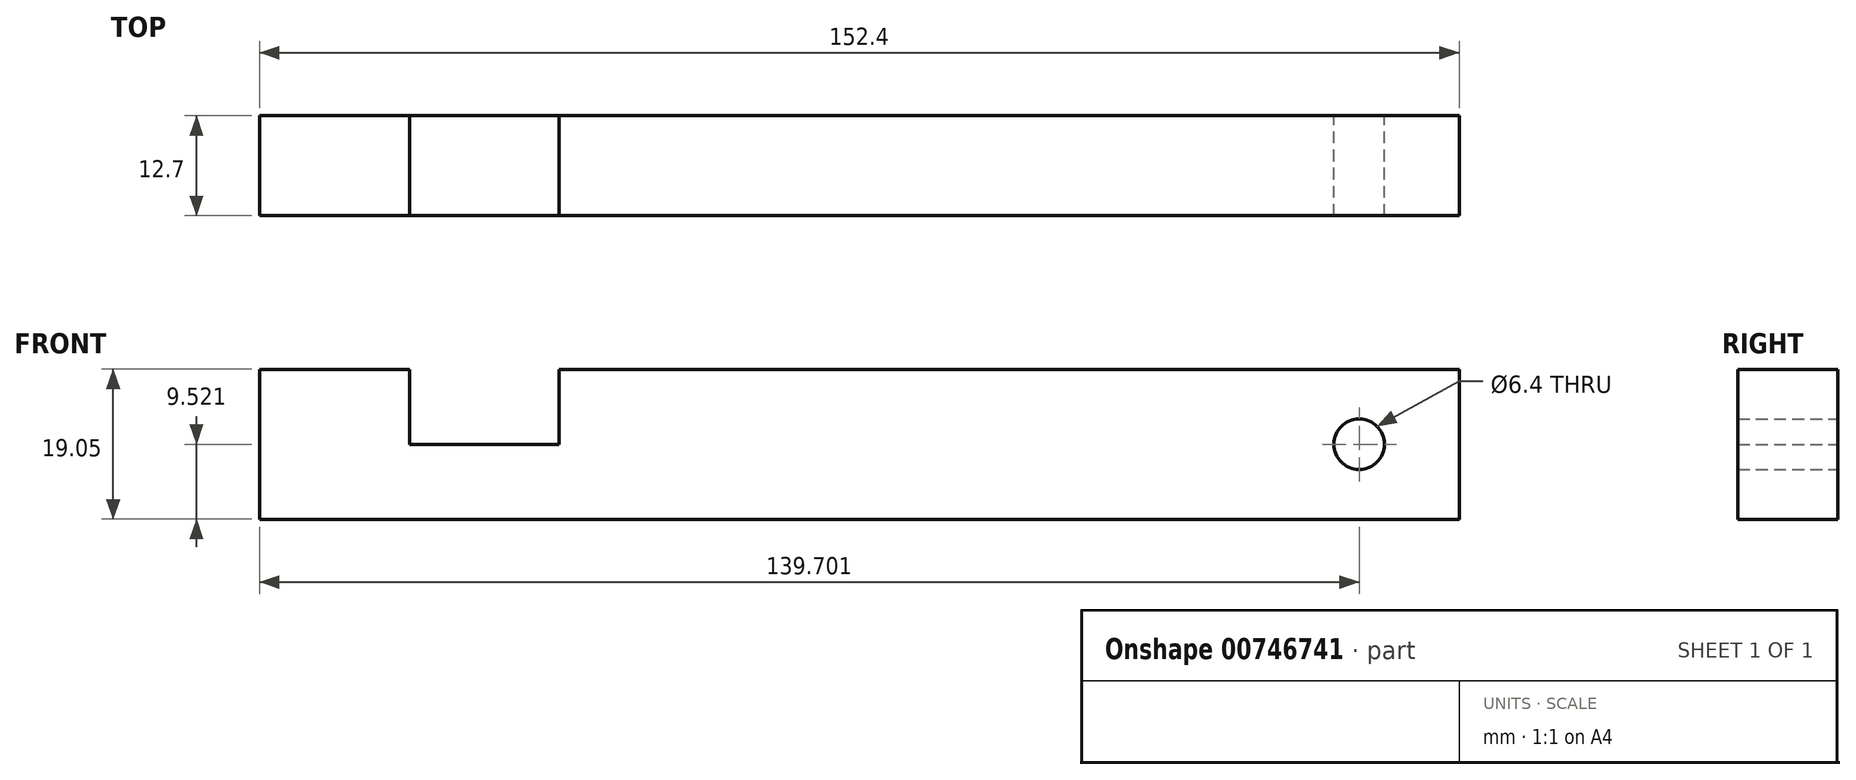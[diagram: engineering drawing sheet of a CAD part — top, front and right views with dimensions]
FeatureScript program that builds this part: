
annotation { "Feature Type Name" : "Feature", "Feature Type Description" : "" }
export const myFeature = defineFeature(function(context is Context, id is Id, definition is map)
    precondition{}
    {
        {
            var Q0;
            Q0=qCreatedBy(makeId("Front.planeOp"),FACE);
            var sketch = newSketch(context, id + "F0", { "sketchPlane" : qUnion([Q0])});
            skLineSegment(sketch, "E0.bottom", {"start": v(69.3, 3.94) * mm, "end": v(-83.1, 3.94) * mm});
            skLineSegment(sketch, "E0.top", {"start": v(69.3, 22.99) * mm, "end": v(-83.1, 22.99) * mm});
            skLineSegment(sketch, "E0.left", {"start": v(69.3, 3.94) * mm, "end": v(69.3, 22.99) * mm});
            skLineSegment(sketch, "E0.right", {"start": v(-83.1, 3.94) * mm, "end": v(-83.1, 22.99) * mm});
            skLineSegment(sketch, "E1.bottom", {"start": v(-64.05, 22.99) * mm, "end": v(-45, 22.99) * mm});
            skLineSegment(sketch, "E1.top", {"start": v(-64.05, 13.46) * mm, "end": v(-45, 13.46) * mm});
            skLineSegment(sketch, "E1.left", {"start": v(-64.05, 22.99) * mm, "end": v(-64.05, 13.46) * mm});
            skLineSegment(sketch, "E1.right", {"start": v(-45, 22.99) * mm, "end": v(-45, 13.46) * mm});
            skCircle(sketch, "E2", {"center": v(56.6, 13.46) * mm, "radius": 3.2 * mm});
            skSolve(sketch);
        }
        {
            var Q0;
            Q0=makeQuery(id+"F0.imprint","IMPRINT",FACE,{"disambiguationData":[TD([[makeQuery(id+"F0.imprint","IMPRINT",EDGE,{"derivedFrom":sQuery(id+"F0.wireOp",EDGE,"E0.bottom")}),-1.0]])]});
            extrude(context, id + "F1", {"entities" : qUnion([Q0]), "depth" : 12.7 * mm, "offsetDistance" : 25.4 * mm});
        }
    });
